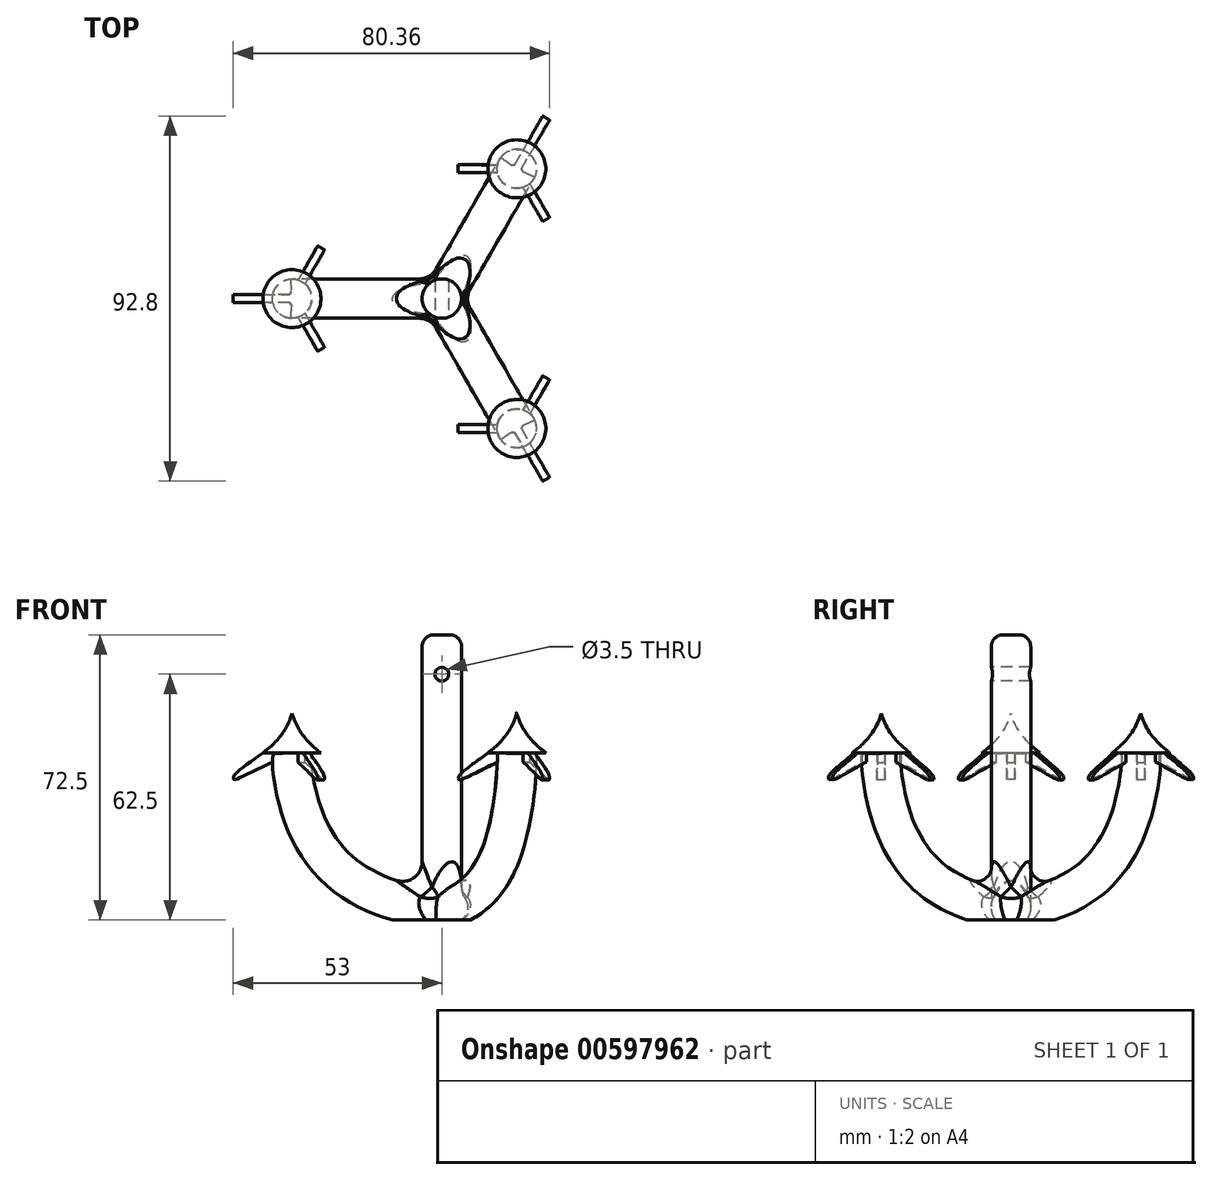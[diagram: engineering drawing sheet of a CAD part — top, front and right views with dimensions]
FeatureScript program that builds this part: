
annotation { "Feature Type Name" : "Feature", "Feature Type Description" : "" }
export const myFeature = defineFeature(function(context is Context, id is Id, definition is map)
    precondition{}
    {
        {
            var Q0;
            Q0=qCreatedBy(makeId("Front.planeOp"),FACE);
            var sketch = newSketch(context, id + "F0", { "sketchPlane" : qUnion([Q0])});
            skPoint(sketch, "E0.first.point", {"position": v(0, 0) * mm});
            skPoint(sketch, "E0.second.point", {"position": v(0, 74.32) * mm});
            skPoint(sketch, "E0.third.point", {"position": v(37.06, 39.93) * mm});
            skLineSegment(sketch, "E1", {"start": v(0, 0) * mm, "end": v(0, 74.32) * mm});
            skFitSpline(sketch, "E2", {"points": [v(0, 0) * mm, v(-22, 7) * mm, v(-34, 21) * mm, v(-38, 36) * mm, v(-38, 40) * mm], "startDerivative": vector(-75.12, 9.39) * mm, "endDerivative": vector(1.9, 22.03) * mm});
            skFitSpline(sketch, "E3", {"points": [v(-38.04, 50.03) * mm, v(-42.6, 42.46) * mm, v(-52.62, 34.44) * mm, v(-52.92, 33.33) * mm, v(-51.23, 33.69) * mm, v(-38.08, 39.02) * mm], "startDerivative": vector(-7.13, -25.47) * mm, "endDerivative": vector(21.26, -4.26) * mm});
            skLineSegment(sketch, "E4", {"start": v(-38.04, 50.03) * mm, "end": v(-38.08, 39.02) * mm});
            skLineSegment(sketch, "E5", {"start": v(-38, 40) * mm, "end": v(-45.45, 40) * mm});
            skCircle(sketch, "E6", {"center": v(0, 60) * mm, "radius": 1.75 * mm});
            skSolve(sketch);
        }
        {
            var Q0;
            Q0=qCreatedBy(makeId("Right.planeOp"),FACE);
            var sketch = newSketch(context, id + "F1", { "sketchPlane" : qUnion([Q0])});
            skCircle(sketch, "E7", {"center": v(0, 0) * mm, "radius": 5 * mm});
            skSolve(sketch);
        }
        {
            var Q0;
            Q0=makeQuery(id+"F1.imprint","IMPRINT",FACE,{"disambiguationData":[TD([[makeQuery(id+"F1.imprint","IMPRINT",EDGE,{"derivedFrom":sQuery(id+"F1.wireOp",EDGE,"E7")}),1.0]])]});
            var Q1;
            Q1=sQuery(id+"F0.wireOp",EDGE,"E2");
            sweep(context, id + "F2", {"profiles" : qUnion([Q0]), "path" : qUnion([Q1])});
        }
        {
            var Q0;
            {var subQ0=sQuery(id+"F0.wireOp",EDGE,"E4");var subQ1=sQuery(id+"F0.wireOp",EDGE,"E3");var subQ2=makeQuery(id+"F0.imprint","INTERSECT",VERTEX,{"disambiguationData":[OD(0.0)],"derivedFrom":[subQ1,subQ0]});Q0=makeQuery(id+"F0.imprint","IMPRINT",FACE,{"disambiguationData":[TD([[makeQuery(id+"F0.imprint","IMPRINT",EDGE,{"disambiguationData":[TD([[subQ2,-1.0]])],"derivedFrom":subQ1}),1.0]])]});}
            var Q1;
            Q1=sQuery(id+"F0.wireOp",EDGE,"E4");
            revolve(context, id + "F3", {"operationType" : NewBodyOperationType.ADD, "entities" : qUnion([Q0]), "axis" : qUnion([Q1]), "revolveType" : RevolveType.FULL});
        }
        {
            var Q0;
            {var subQ0=sQuery(id+"F0.wireOp",EDGE,"E4");var subQ1=sQuery(id+"F0.wireOp",EDGE,"E3");var subQ2=makeQuery(id+"F0.imprint","INTERSECT",VERTEX,{"disambiguationData":[OD(1.0)],"derivedFrom":[subQ1,subQ0]});Q0=makeQuery(id+"F0.imprint","IMPRINT",FACE,{"disambiguationData":[TD([[makeQuery(id+"F0.imprint","IMPRINT",EDGE,{"disambiguationData":[TD([[subQ2,1.0]])],"derivedFrom":subQ1}),1.0]])]});}
            extrude(context, id + "F4", {"entities" : qUnion([Q0]), "depth" : 1 * mm, "offsetDistance" : 25 * mm, "hasSecondDirection" : true, "secondDirectionOppositeDirection" : true, "secondDirectionDepth" : 1 * mm});
        }
        {
            var Q0;
            Q0=makeQuery(id+"F4.opExtrude","SWEPT_BODY",BODY,{"disambiguationData":[OSD([sQuery(id+"F0.wireOp",EDGE,"E3"),sQuery(id+"F0.wireOp",EDGE,"E4"),sQuery(id+"F0.wireOp",EDGE,"E5")])]});
            var Q1;
            Q1=sQuery(id+"F0.wireOp",EDGE,"E4");
            circularPattern(context, id + "F5", {"operationType" : NewBodyOperationType.ADD, "entities" : qUnion([Q0]), "axis" : qUnion([Q1]), "angle" : 360 * degree, "instanceCount" : 3, "equalSpace" : true});
        }
        {
            var Q0;
            Q0=makeQuery(id+"F2.opSweep","SWEPT_BODY",BODY,{"disambiguationData":[OSD([sQuery(id+"F0.wireOp",EDGE,"E2"),sQuery(id+"F1.wireOp",EDGE,"E7")])]});
            var Q1;
            Q1=sQuery(id+"F0.wireOp",EDGE,"E1");
            circularPattern(context, id + "F6", {"operationType" : NewBodyOperationType.ADD, "entities" : qUnion([Q0]), "axis" : qUnion([Q1]), "angle" : 360 * degree, "instanceCount" : 3, "equalSpace" : true});
        }
        {
            var Q0;
            Q0=qCreatedBy(makeId("Top.planeOp"),FACE);
            var sketch = newSketch(context, id + "F7", { "sketchPlane" : qUnion([Q0])});
            skCircle(sketch, "E8", {"center": v(0, 0) * mm, "radius": 5 * mm});
            skCircle(sketch, "E9", {"center": v(0, 0) * mm, "radius": 24 * mm});
            skSolve(sketch);
        }
        {
            var Q0;
            Q0=makeQuery(id+"F7.imprint","IMPRINT",FACE,{"disambiguationData":[TD([[makeQuery(id+"F7.imprint","IMPRINT",EDGE,{"derivedFrom":sQuery(id+"F7.wireOp",EDGE,"E8")}),1.0]])]});
            extrude(context, id + "F8", {"entities" : qUnion([Q0]), "operationType" : NewBodyOperationType.ADD, "depth" : 70 * mm, "offsetDistance" : 25 * mm});
        }
        {
            var Q0;
            Q0=makeQuery(id+"F8.opExtrude","CAP_EDGE",EDGE,{"disambiguationData":[OSD([sQuery(id+"F7.wireOp",EDGE,"E8")])],"isStart":false});
            fillet(context, id + "F9", {"entities" : qUnion([Q0]), "radius" : 3 * mm, "tangentPropagation" : true, "allowEdgeOverflow" : false});
        }
        {
            var Q0;
            {var subQ0=sQuery(id+"F0.wireOp",EDGE,"E6");var subQ1=sQuery(id+"F0.wireOp",EDGE,"E1");var subQ2=makeQuery(id+"F0.imprint","INTERSECT",VERTEX,{"disambiguationData":[OD(0.0)],"derivedFrom":[subQ1,subQ0]});Q0=makeQuery(id+"F0.imprint","IMPRINT",FACE,{"disambiguationData":[TD([[makeQuery(id+"F0.imprint","IMPRINT",EDGE,{"disambiguationData":[TD([[subQ2,-1.0]])],"derivedFrom":subQ1}),-1.0]])]});}
            var Q1;
            {var subQ0=sQuery(id+"F0.wireOp",EDGE,"E6");var subQ1=sQuery(id+"F0.wireOp",EDGE,"E1");var subQ2=makeQuery(id+"F0.imprint","INTERSECT",VERTEX,{"disambiguationData":[OD(0.0)],"derivedFrom":[subQ1,subQ0]});Q1=makeQuery(id+"F0.imprint","IMPRINT",FACE,{"disambiguationData":[TD([[makeQuery(id+"F0.imprint","IMPRINT",EDGE,{"disambiguationData":[TD([[subQ2,-1.0]])],"derivedFrom":subQ1}),1.0]])]});}
            extrude(context, id + "F10", {"entities" : qUnion([Q0, Q1]), "operationType" : NewBodyOperationType.REMOVE, "endBound" : BoundingType.SYMMETRIC, "oppositeDirection" : true, "depth" : 25 * mm, "offsetDistance" : 25 * mm});
        }
        {
            var Q0;
            Q0=makeQuery(id+"F7.imprint","IMPRINT",FACE,{"disambiguationData":[TD([[makeQuery(id+"F7.imprint","IMPRINT",EDGE,{"derivedFrom":sQuery(id+"F7.wireOp",EDGE,"E8")}),-1.0]])]});
            var Q1;
            Q1=makeQuery(id+"F7.imprint","IMPRINT",FACE,{"disambiguationData":[TD([[makeQuery(id+"F7.imprint","IMPRINT",EDGE,{"derivedFrom":sQuery(id+"F7.wireOp",EDGE,"E8")}),1.0]])]});
            extrude(context, id + "F11", {"entities" : qUnion([Q0, Q1]), "operationType" : NewBodyOperationType.REMOVE, "oppositeDirection" : true, "depth" : 25 * mm, "offsetDistance" : 25 * mm, "hasSecondDirection" : true, "secondDirectionOppositeDirection" : true, "secondDirectionDepth" : 2.5 * mm});
        }
        {
            var Q0;
            {var subQ0=sQuery(id+"F0.wireOp",EDGE,"E5");var subQ1=sQuery(id+"F0.wireOp",EDGE,"E4");var subQ2=sQuery(id+"F0.wireOp",EDGE,"E3");var subQ3=makeQuery(id+"F4.opExtrude","CAP_FACE",FACE,{"disambiguationData":[OSD([subQ2,subQ1,subQ0])],"isStart":false});var subQ4=makeQuery(id+"F4.opExtrude","CAP_FACE",FACE,{"disambiguationData":[OSD([subQ2,subQ1,subQ0])],"isStart":true});var subQ5=makeQuery(id+"F4.opExtrude","SWEPT_FACE",FACE,{"disambiguationData":[OSD([subQ2])]});var subQ6=sQuery(id+"F1.wireOp",EDGE,"E7");var subQ7=makeQuery(id+"F2.opSweep","SWEPT_FACE",FACE,{"disambiguationData":[OSD([sQuery(id+"F0.wireOp",EDGE,"E2"),subQ6])]});var subQ8=subQ7;var subQ9=makeQuery(id+"F6.opPattern","COPY",FACE,{"derivedFrom":subQ8,"instanceName":"2"});var subQ10=makeQuery(id+"F2.opSweep","CAP_FACE",FACE,{"disambiguationData":[OSD([sQuery(id+"F0.wireOp",VERTEX,"E2.start"),subQ6])],"isStart":true});var subQ11=makeQuery(id+"F5.opPattern","COPY",FACE,{"derivedFrom":subQ5,"instanceName":"1"});var subQ12=makeQuery(id+"F3.opRevolve","SWEPT_FACE",FACE,{"disambiguationData":[OSD([subQ2])]});var subQ13=makeQuery(id+"F2.opSweep","CAP_FACE",FACE,{"disambiguationData":[OSD([sQuery(id+"F0.wireOp",VERTEX,"E2.end"),subQ6])],"isStart":false});var subQ15=makeQuery(id+"F5.opPattern","COPY",FACE,{"derivedFrom":subQ3,"instanceName":"1"});var subQ17=makeQuery(id+"F3.opRevolve","SWEPT_FACE",FACE,{"disambiguationData":[OSD([subQ0])]});var subQ18=subQ17;var subQ19=makeQuery(id+"F5.opPattern","COPY",FACE,{"derivedFrom":subQ4,"instanceName":"1"});var subQ20=makeQuery(id+"F5.opPattern","COPY",FACE,{"derivedFrom":subQ5,"instanceName":"2"});var subQ21=makeQuery(id+"F5.opPattern","COPY",FACE,{"derivedFrom":subQ3,"instanceName":"2"});var subQ22=subQ13;var subQ23=makeQuery(id+"F5.opPattern","COPY",FACE,{"derivedFrom":subQ4,"instanceName":"2"});Q0=makeQuery(id+"F8.boolean.opBoolean","INTERSECT",EDGE,{"derivedFrom":[makeQuery(id+"F6.boolean.opBoolean","SPLIT",FACE,{"disambiguationData":[TD([subQ10,subQ7,makeQuery(id+"F6.opPattern","COPY",FACE,{"derivedFrom":subQ10,"instanceName":"1"}),makeQuery(id+"F6.opPattern","COPY",FACE,{"derivedFrom":subQ8,"instanceName":"1"}),makeQuery(id+"F6.opPattern","COPY",FACE,{"derivedFrom":subQ10,"instanceName":"2"}),subQ9,makeQuery(id+"F6.opPattern","COPY",FACE,{"derivedFrom":subQ5,"instanceName":"2"}),makeQuery(id+"F6.opPattern","COPY",FACE,{"derivedFrom":subQ4,"instanceName":"2"}),makeQuery(id+"F6.opPattern","COPY",FACE,{"derivedFrom":subQ3,"instanceName":"2"}),makeQuery(id+"F6.opPattern","COPY",FACE,{"derivedFrom":subQ11,"instanceName":"2"}),makeQuery(id+"F6.opPattern","COPY",FACE,{"derivedFrom":subQ19,"instanceName":"2"}),makeQuery(id+"F6.opPattern","COPY",FACE,{"derivedFrom":subQ20,"instanceName":"2"}),makeQuery(id+"F6.opPattern","COPY",FACE,{"derivedFrom":subQ21,"instanceName":"2"}),makeQuery(id+"F6.opPattern","COPY",FACE,{"derivedFrom":makeQuery(id+"F5.boolean.opBoolean","SPLIT",FACE,{"disambiguationData":[TD([subQ4])],"derivedFrom":subQ22}),"instanceName":"2"}),makeQuery(id+"F6.opPattern","COPY",FACE,{"derivedFrom":makeQuery(id+"F5.boolean.opBoolean","SPLIT",FACE,{"disambiguationData":[TD([subQ3])],"derivedFrom":subQ22}),"instanceName":"2"}),makeQuery(id+"F6.opPattern","COPY",FACE,{"derivedFrom":makeQuery(id+"F5.boolean.opBoolean","SPLIT",FACE,{"disambiguationData":[TD([subQ19])],"derivedFrom":subQ18}),"instanceName":"2"}),makeQuery(id+"F6.opPattern","COPY",FACE,{"derivedFrom":makeQuery(id+"F5.boolean.opBoolean","SPLIT",FACE,{"disambiguationData":[TD([subQ4])],"derivedFrom":subQ18}),"instanceName":"2"}),makeQuery(id+"F6.opPattern","COPY",FACE,{"derivedFrom":makeQuery(id+"F5.boolean.opBoolean","SPLIT",FACE,{"disambiguationData":[TD([subQ3])],"derivedFrom":subQ18}),"instanceName":"2"}),makeQuery(id+"F6.opPattern","COPY",FACE,{"derivedFrom":makeQuery(id+"F5.boolean.opBoolean","SPLIT",FACE,{"disambiguationData":[TD([subQ12])],"derivedFrom":subQ15}),"instanceName":"2"}),makeQuery(id+"F6.opPattern","COPY",FACE,{"derivedFrom":makeQuery(id+"F5.boolean.opBoolean","SPLIT",FACE,{"disambiguationData":[TD([subQ12])],"derivedFrom":subQ23}),"instanceName":"2"})])],"derivedFrom":subQ9}),makeQuery(id+"F8.opExtrude","SWEPT_FACE",FACE,{"disambiguationData":[OSD([sQuery(id+"F7.wireOp",EDGE,"E8")])]})]});}
            var Q1;
            {var subQ0=sQuery(id+"F0.wireOp",EDGE,"E3");var subQ1=makeQuery(id+"F4.opExtrude","SWEPT_FACE",FACE,{"disambiguationData":[OSD([subQ0])]});var subQ2=makeQuery(id+"F5.opPattern","COPY",FACE,{"derivedFrom":subQ1,"instanceName":"2"});var subQ3=sQuery(id+"F0.wireOp",EDGE,"E5");var subQ4=sQuery(id+"F0.wireOp",EDGE,"E4");var subQ5=makeQuery(id+"F4.opExtrude","CAP_FACE",FACE,{"disambiguationData":[OSD([subQ0,subQ4,subQ3])],"isStart":true});var subQ6=makeQuery(id+"F5.opPattern","COPY",FACE,{"derivedFrom":subQ5,"instanceName":"1"});var subQ7=makeQuery(id+"F5.opPattern","COPY",FACE,{"derivedFrom":subQ1,"instanceName":"1"});var subQ8=makeQuery(id+"F4.opExtrude","CAP_FACE",FACE,{"disambiguationData":[OSD([subQ0,subQ4,subQ3])],"isStart":false});var subQ9=sQuery(id+"F1.wireOp",EDGE,"E7");var subQ10=makeQuery(id+"F2.opSweep","SWEPT_FACE",FACE,{"disambiguationData":[OSD([sQuery(id+"F0.wireOp",EDGE,"E2"),subQ9])]});var subQ11=subQ10;var subQ12=makeQuery(id+"F2.opSweep","CAP_FACE",FACE,{"disambiguationData":[OSD([sQuery(id+"F0.wireOp",VERTEX,"E2.start"),subQ9])],"isStart":true});var subQ13=makeQuery(id+"F6.opPattern","COPY",FACE,{"derivedFrom":subQ11,"instanceName":"1"});var subQ14=makeQuery(id+"F5.opPattern","COPY",FACE,{"derivedFrom":subQ8,"instanceName":"2"});var subQ15=makeQuery(id+"F3.opRevolve","SWEPT_FACE",FACE,{"disambiguationData":[OSD([subQ3])]});var subQ16=makeQuery(id+"F5.opPattern","COPY",FACE,{"derivedFrom":subQ8,"instanceName":"1"});var subQ17=makeQuery(id+"F2.opSweep","CAP_FACE",FACE,{"disambiguationData":[OSD([sQuery(id+"F0.wireOp",VERTEX,"E2.end"),subQ9])],"isStart":false});var subQ18=subQ17;var subQ19=makeQuery(id+"F5.opPattern","COPY",FACE,{"derivedFrom":subQ5,"instanceName":"2"});var subQ22=makeQuery(id+"F3.opRevolve","SWEPT_FACE",FACE,{"disambiguationData":[OSD([subQ0])]});var subQ24=subQ15;Q1=makeQuery(id+"F8.boolean.opBoolean","INTERSECT",EDGE,{"derivedFrom":[makeQuery(id+"F6.boolean.opBoolean","SPLIT",FACE,{"disambiguationData":[TD([subQ12,subQ10,makeQuery(id+"F6.opPattern","COPY",FACE,{"derivedFrom":subQ12,"instanceName":"1"}),subQ13,makeQuery(id+"F6.opPattern","COPY",FACE,{"derivedFrom":subQ1,"instanceName":"1"}),makeQuery(id+"F6.opPattern","COPY",FACE,{"derivedFrom":subQ5,"instanceName":"1"}),makeQuery(id+"F6.opPattern","COPY",FACE,{"derivedFrom":subQ8,"instanceName":"1"}),makeQuery(id+"F6.opPattern","COPY",FACE,{"derivedFrom":subQ7,"instanceName":"1"}),makeQuery(id+"F6.opPattern","COPY",FACE,{"derivedFrom":subQ6,"instanceName":"1"}),makeQuery(id+"F6.opPattern","COPY",FACE,{"derivedFrom":subQ2,"instanceName":"1"}),makeQuery(id+"F6.opPattern","COPY",FACE,{"derivedFrom":subQ14,"instanceName":"1"}),makeQuery(id+"F6.opPattern","COPY",FACE,{"derivedFrom":makeQuery(id+"F5.boolean.opBoolean","SPLIT",FACE,{"disambiguationData":[TD([subQ5])],"derivedFrom":subQ18}),"instanceName":"1"}),makeQuery(id+"F6.opPattern","COPY",FACE,{"derivedFrom":makeQuery(id+"F5.boolean.opBoolean","SPLIT",FACE,{"disambiguationData":[TD([subQ8])],"derivedFrom":subQ18}),"instanceName":"1"}),makeQuery(id+"F6.opPattern","COPY",FACE,{"derivedFrom":makeQuery(id+"F5.boolean.opBoolean","SPLIT",FACE,{"disambiguationData":[TD([subQ6])],"derivedFrom":subQ24}),"instanceName":"1"}),makeQuery(id+"F6.opPattern","COPY",FACE,{"derivedFrom":makeQuery(id+"F5.boolean.opBoolean","SPLIT",FACE,{"disambiguationData":[TD([subQ5])],"derivedFrom":subQ24}),"instanceName":"1"}),makeQuery(id+"F6.opPattern","COPY",FACE,{"derivedFrom":makeQuery(id+"F5.boolean.opBoolean","SPLIT",FACE,{"disambiguationData":[TD([subQ8])],"derivedFrom":subQ24}),"instanceName":"1"}),makeQuery(id+"F6.opPattern","COPY",FACE,{"derivedFrom":makeQuery(id+"F5.boolean.opBoolean","SPLIT",FACE,{"disambiguationData":[TD([subQ22])],"derivedFrom":subQ16}),"instanceName":"1"}),makeQuery(id+"F6.opPattern","COPY",FACE,{"derivedFrom":makeQuery(id+"F5.boolean.opBoolean","SPLIT",FACE,{"disambiguationData":[TD([subQ22])],"derivedFrom":subQ19}),"instanceName":"1"}),makeQuery(id+"F6.opPattern","COPY",FACE,{"derivedFrom":subQ12,"instanceName":"2"}),makeQuery(id+"F6.opPattern","COPY",FACE,{"derivedFrom":subQ11,"instanceName":"2"})])],"derivedFrom":subQ13}),makeQuery(id+"F8.opExtrude","SWEPT_FACE",FACE,{"disambiguationData":[OSD([sQuery(id+"F7.wireOp",EDGE,"E8")])]})]});}
            var Q2;
            {var subQ0=sQuery(id+"F0.wireOp",EDGE,"E5");var subQ1=sQuery(id+"F0.wireOp",EDGE,"E4");var subQ2=sQuery(id+"F0.wireOp",EDGE,"E3");var subQ3=makeQuery(id+"F4.opExtrude","CAP_FACE",FACE,{"disambiguationData":[OSD([subQ2,subQ1,subQ0])],"isStart":false});var subQ4=makeQuery(id+"F4.opExtrude","CAP_FACE",FACE,{"disambiguationData":[OSD([subQ2,subQ1,subQ0])],"isStart":true});var subQ5=sQuery(id+"F1.wireOp",EDGE,"E7");var subQ6=makeQuery(id+"F2.opSweep","CAP_FACE",FACE,{"disambiguationData":[OSD([sQuery(id+"F0.wireOp",VERTEX,"E2.start"),subQ5])],"isStart":true});var subQ7=makeQuery(id+"F4.opExtrude","SWEPT_FACE",FACE,{"disambiguationData":[OSD([subQ2])]});var subQ8=makeQuery(id+"F2.opSweep","SWEPT_FACE",FACE,{"disambiguationData":[OSD([sQuery(id+"F0.wireOp",EDGE,"E2"),subQ5])]});var subQ9=subQ8;Q2=makeQuery(id+"F8.boolean.opBoolean","INTERSECT",EDGE,{"derivedFrom":[makeQuery(id+"F6.boolean.opBoolean","SPLIT",FACE,{"disambiguationData":[TD([subQ6,makeQuery(id+"F2.opSweep","CAP_FACE",FACE,{"disambiguationData":[OSD([sQuery(id+"F0.wireOp",VERTEX,"E2.end"),subQ5])],"isStart":false}),subQ8,makeQuery(id+"F3.opRevolve","SWEPT_FACE",FACE,{"disambiguationData":[OSD([subQ0])]}),subQ7,subQ4,subQ3,makeQuery(id+"F5.opPattern","COPY",FACE,{"derivedFrom":subQ7,"instanceName":"1"}),makeQuery(id+"F5.opPattern","COPY",FACE,{"derivedFrom":subQ4,"instanceName":"1"}),makeQuery(id+"F5.opPattern","COPY",FACE,{"derivedFrom":subQ3,"instanceName":"1"}),makeQuery(id+"F5.opPattern","COPY",FACE,{"derivedFrom":subQ7,"instanceName":"2"}),makeQuery(id+"F5.opPattern","COPY",FACE,{"derivedFrom":subQ4,"instanceName":"2"}),makeQuery(id+"F5.opPattern","COPY",FACE,{"derivedFrom":subQ3,"instanceName":"2"}),makeQuery(id+"F6.opPattern","COPY",FACE,{"derivedFrom":subQ6,"instanceName":"1"}),makeQuery(id+"F6.opPattern","COPY",FACE,{"derivedFrom":subQ9,"instanceName":"1"}),makeQuery(id+"F6.opPattern","COPY",FACE,{"derivedFrom":subQ6,"instanceName":"2"}),makeQuery(id+"F6.opPattern","COPY",FACE,{"derivedFrom":subQ9,"instanceName":"2"})])],"derivedFrom":subQ9}),makeQuery(id+"F8.opExtrude","SWEPT_FACE",FACE,{"disambiguationData":[OSD([sQuery(id+"F7.wireOp",EDGE,"E8")])]})]});}
            var Q3;
            {var subQ0=makeQuery(id+"F2.opSweep","SWEPT_FACE",FACE,{"disambiguationData":[OSD([sQuery(id+"F0.wireOp",EDGE,"E2"),sQuery(id+"F1.wireOp",EDGE,"E7")])]});Q3=makeQuery(id+"F6.boolean.opBoolean","INTERSECT",EDGE,{"disambiguationData":[OD(0.0)],"derivedFrom":[subQ0,makeQuery(id+"F6.opPattern","COPY",FACE,{"derivedFrom":subQ0,"instanceName":"1"})]});}
            var Q4;
            {var subQ0=makeQuery(id+"F2.opSweep","SWEPT_FACE",FACE,{"disambiguationData":[OSD([sQuery(id+"F0.wireOp",EDGE,"E2"),sQuery(id+"F1.wireOp",EDGE,"E7")])]});Q4=makeQuery(id+"F6.boolean.opBoolean","INTERSECT",EDGE,{"disambiguationData":[OD(0.0)],"derivedFrom":[makeQuery(id+"F6.opPattern","COPY",FACE,{"derivedFrom":subQ0,"instanceName":"1"}),makeQuery(id+"F6.opPattern","COPY",FACE,{"derivedFrom":subQ0,"instanceName":"2"})]});}
            var Q5;
            {var subQ0=makeQuery(id+"F2.opSweep","SWEPT_FACE",FACE,{"disambiguationData":[OSD([sQuery(id+"F0.wireOp",EDGE,"E2"),sQuery(id+"F1.wireOp",EDGE,"E7")])]});Q5=makeQuery(id+"F6.boolean.opBoolean","INTERSECT",EDGE,{"disambiguationData":[OD(0.0)],"derivedFrom":[subQ0,makeQuery(id+"F6.opPattern","COPY",FACE,{"derivedFrom":subQ0,"instanceName":"2"})]});}
            fillet(context, id + "F12", {"entities" : qUnion([Q0, Q1, Q2, Q3, Q4, Q5]), "radius" : 5 * mm, "tangentPropagation" : true, "allowEdgeOverflow" : false});
        }
    });
